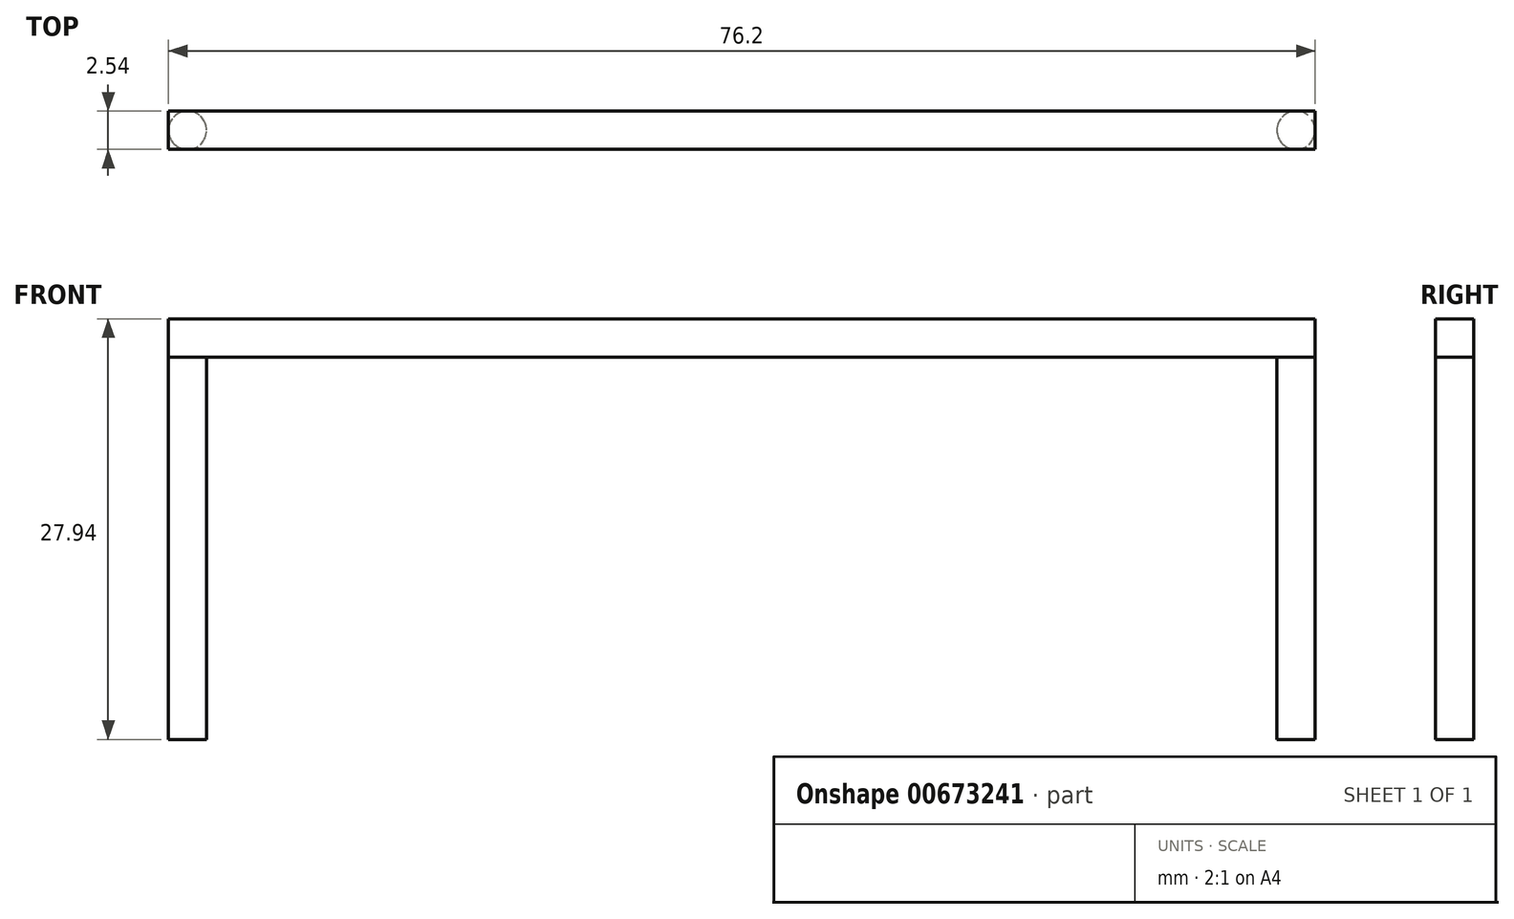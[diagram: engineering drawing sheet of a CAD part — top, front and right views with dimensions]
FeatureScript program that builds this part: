
annotation { "Feature Type Name" : "Feature", "Feature Type Description" : "" }
export const myFeature = defineFeature(function(context is Context, id is Id, definition is map)
    precondition{}
    {
        {
            var Q0;
            Q0=qCreatedBy(makeId("Front.planeOp"),FACE);
            var sketch = newSketch(context, id + "F0", { "sketchPlane" : qUnion([Q0])});
            skLineSegment(sketch, "E0.bottom", {"start": v(-38.1, 0) * mm, "end": v(-36.83, 0) * mm});
            skLineSegment(sketch, "E0.top", {"start": v(-38.1, 25.4) * mm, "end": v(-36.83, 25.4) * mm});
            skLineSegment(sketch, "E0.left", {"start": v(-38.1, 0) * mm, "end": v(-38.1, 25.4) * mm});
            skLineSegment(sketch, "E0.right", {"start": v(-36.83, 0) * mm, "end": v(-36.83, 25.4) * mm});
            skLineSegment(sketch, "E1.bottom", {"start": v(36.83, 0) * mm, "end": v(38.1, 0) * mm});
            skLineSegment(sketch, "E1.top", {"start": v(36.83, 25.4) * mm, "end": v(38.1, 25.4) * mm});
            skLineSegment(sketch, "E1.left", {"start": v(36.83, 0) * mm, "end": v(36.83, 25.4) * mm});
            skLineSegment(sketch, "E1.right", {"start": v(38.1, 0) * mm, "end": v(38.1, 25.4) * mm});
            skLineSegment(sketch, "E2.right", {"start": v(38.1, 25.4) * mm, "end": v(38.1, 25.4) * mm});
            skLineSegment(sketch, "E3.bottom", {"start": v(-38.1, 25.4) * mm, "end": v(38.1, 25.4) * mm});
            skLineSegment(sketch, "E3.top", {"start": v(-38.1, 27.94) * mm, "end": v(38.1, 27.94) * mm});
            skLineSegment(sketch, "E3.left", {"start": v(-38.1, 25.4) * mm, "end": v(-38.1, 27.94) * mm});
            skLineSegment(sketch, "E3.right", {"start": v(38.1, 25.4) * mm, "end": v(38.1, 27.94) * mm});
            skSolve(sketch);
        }
        {
            var Q0;
            Q0=makeQuery(id+"F0.imprint","IMPRINT",FACE,{"disambiguationData":[TD([[makeQuery(id+"F0.imprint","IMPRINT",EDGE,{"derivedFrom":sQuery(id+"F0.wireOp",EDGE,"E3.top")}),-1.0]])]});
            extrude(context, id + "F1", {"entities" : qUnion([Q0]), "endBound" : BoundingType.SYMMETRIC, "depth" : 2.54 * mm, "offsetDistance" : 25.4 * mm});
        }
        {
            var Q0;
            Q0=makeQuery(id+"F0.imprint","IMPRINT",FACE,{"disambiguationData":[TD([[makeQuery(id+"F0.imprint","IMPRINT",EDGE,{"derivedFrom":sQuery(id+"F0.wireOp",EDGE,"E0.bottom")}),1.0]])]});
            var Q1;
            Q1=sQuery(id+"F0.wireOp",EDGE,"E0.right");
            revolve(context, id + "F2", {"operationType" : NewBodyOperationType.ADD, "entities" : qUnion([Q0]), "axis" : qUnion([Q1]), "revolveType" : RevolveType.FULL});
        }
        {
            var Q0;
            Q0=makeQuery(id+"F0.imprint","IMPRINT",FACE,{"disambiguationData":[TD([[makeQuery(id+"F0.imprint","IMPRINT",EDGE,{"derivedFrom":sQuery(id+"F0.wireOp",EDGE,"E1.bottom")}),1.0]])]});
            var Q1;
            Q1=sQuery(id+"F0.wireOp",EDGE,"E1.left");
            revolve(context, id + "F3", {"operationType" : NewBodyOperationType.ADD, "entities" : qUnion([Q0]), "axis" : qUnion([Q1]), "revolveType" : RevolveType.FULL});
        }
    });
